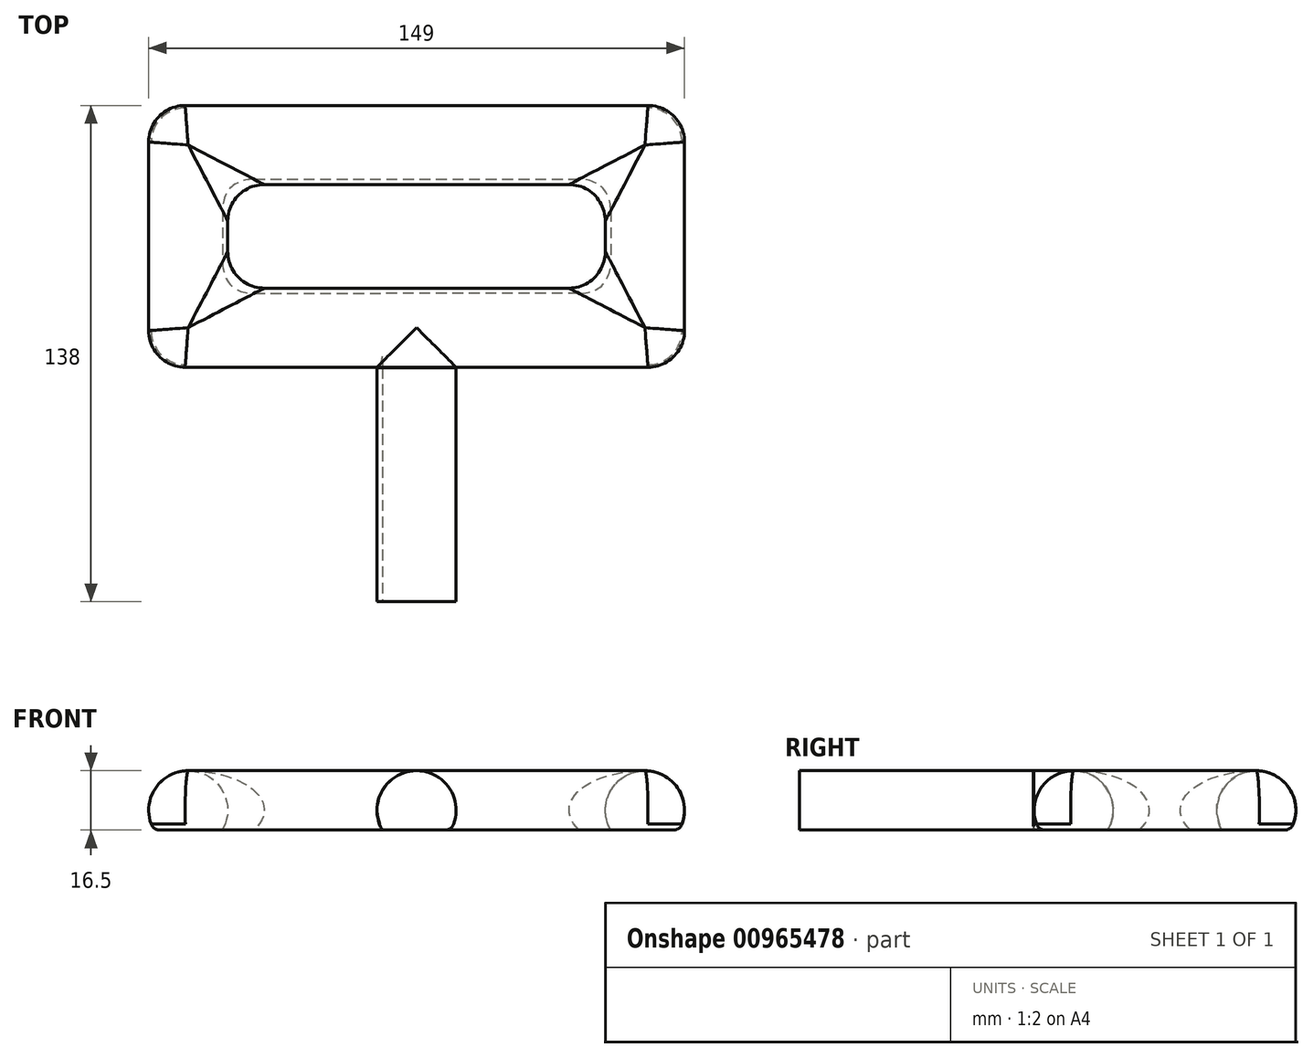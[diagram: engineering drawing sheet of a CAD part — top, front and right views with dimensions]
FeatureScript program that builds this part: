
annotation { "Feature Type Name" : "Feature", "Feature Type Description" : "" }
export const myFeature = defineFeature(function(context is Context, id is Id, definition is map)
    precondition{}
    {
        {
            var Q0;
            Q0=qCreatedBy(makeId("Top.planeOp"),FACE);
            var sketch = newSketch(context, id + "F0", { "sketchPlane" : qUnion([Q0])});
            skLineSegment(sketch, "E0", {"start": v(36.2, -40.03) * mm, "end": v(36.2, 36.17) * mm});
            skLineSegment(sketch, "E1", {"start": v(36.2, 36.17) * mm, "end": v(99.7, 36.17) * mm});
            skLineSegment(sketch, "E2", {"start": v(99.7, 36.17) * mm, "end": v(99.7, 86.97) * mm});
            skLineSegment(sketch, "E3", {"start": v(99.7, 86.97) * mm, "end": v(36.2, 86.97) * mm});
            skLineSegment(sketch, "E4.MirrorCS", {"start": v(36.2, 36.17) * mm, "end": v(-27.3, 36.17) * mm});
            skLineSegment(sketch, "E5.MirrorCS", {"start": v(-27.3, 36.17) * mm, "end": v(-27.3, 86.97) * mm});
            skLineSegment(sketch, "E6.MirrorCS", {"start": v(-27.3, 86.97) * mm, "end": v(36.2, 86.97) * mm});
            skSolve(sketch);
        }
        {
            var Q0;
            Q0=qCreatedBy(makeId("Front.planeOp"),FACE);
            var sketch = newSketch(context, id + "F1", { "sketchPlane" : qUnion([Q0])});
            skPoint(sketch, "E7", {"position": v(36.2, 0) * mm});
            skCircle(sketch, "E8", {"center": v(36.2, 0) * mm, "radius": 11 * mm});
            skLineSegment(sketch, "E9", {"start": v(36.2, 0) * mm, "end": v(36.2, -11) * mm, "construction": true});
            skLineSegment(sketch, "E10", {"start": v(26.68, -5.5) * mm, "end": v(45.73, -5.5) * mm});
            skPoint(sketch, "E10.startSnap0", {"position": v(36.2, -5.5) * mm});
            skPoint(sketch, "E11", {"position": v(29.17, 0) * mm});
            skSolve(sketch);
        }
        {
            var Q0;
            {var subQ0=sQuery(id+"F1.wireOp",EDGE,"E10");Q0=makeQuery(id+"F1.imprint","IMPRINT",FACE,{"disambiguationData":[TD([[makeQuery(id+"F1.imprint","IMPRINT",EDGE,{"derivedFrom":subQ0}),1.0]])]});}
            var Q1;
            Q1=sQuery(id+"F0.wireOp",EDGE,"E0");
            var Q2;
            Q2=sQuery(id+"F0.wireOp",EDGE,"E1");
            var Q3;
            Q3=sQuery(id+"F0.wireOp",EDGE,"E2");
            var Q4;
            Q4=sQuery(id+"F0.wireOp",EDGE,"E3");
            sweep(context, id + "F2", {"profiles" : qUnion([Q0]), "path" : qUnion([Q1, Q2, Q3, Q4])});
        }
        {
            var Q0;
            Q0=qCreatedBy(makeId("Right.planeOp"),FACE);
            cPlane(context, id + "F3", {"entities" : qUnion([Q0]), "cplaneType" : CPlaneType.OFFSET, "offset" : 36.2 * mm, "width" : 152.4 * mm, "height" : 152.4 * mm});
        }
        {
            var Q0;
            Q0=makeQuery(id+"F2.opSweep","SWEPT_BODY",BODY,{"disambiguationData":[OSD([sQuery(id+"F0.wireOp",EDGE,"E3"),sQuery(id+"F1.wireOp",EDGE,"E8"),sQuery(id+"F1.wireOp",EDGE,"E10")])]});
            var Q1;
            Q1=qCreatedBy(id+"F3.planeOp",FACE);
            mirror(context, id + "F4", {"operationType" : NewBodyOperationType.ADD, "entities" : qUnion([Q0]), "mirrorPlane" : qUnion([Q1])});
        }
        {
            var Q0;
            Q0=qCreatedBy(makeId("Front.planeOp"),FACE);
            cPlane(context, id + "F5", {"entities" : qUnion([Q0]), "cplaneType" : CPlaneType.OFFSET, "offset" : 25.12 * mm, "oppositeDirection" : true, "width" : 152.4 * mm, "height" : 152.4 * mm});
        }
        {
            var Q0;
            Q0=qCreatedBy(id+"F5.planeOp",FACE);
            var sketch = newSketch(context, id + "F6", { "sketchPlane" : qUnion([Q0])});
            skCircle(sketch, "E12", {"center": v(36.49, 0) * mm, "radius": 14.97 * mm});
            skLineSegment(sketch, "E13", {"start": v(26.75, -5.42) * mm, "end": v(45.67, -5.42) * mm});
            skArc(sketch, "E14", {"start": v(45.67, -5.42) * mm, "mid": v(36.21, 10.99) * mm, "end": v(26.75, -5.42) * mm});
            skSolve(sketch);
        }
        {
            var Q0;
            Q0=makeQuery(id+"F2.opSweep","MID_CAP_EDGE",EDGE,{"disambiguationData":[OSD([sQuery(id+"F0.wireOp",VERTEX,"E2.start"),sQuery(id+"F1.wireOp",EDGE,"E8")])],"capPos":2.0});
            var Q1;
            Q1=makeQuery(id+"F2.opSweep","MID_CAP_EDGE",EDGE,{"disambiguationData":[OSD([sQuery(id+"F0.wireOp",VERTEX,"E3.start"),sQuery(id+"F1.wireOp",EDGE,"E8")])],"capPos":1.0});
            var Q2;
            Q2=makeQuery(id+"F4.opPattern","COPY",EDGE,{"derivedFrom":makeQuery(id+"F2.opSweep","MID_CAP_EDGE",EDGE,{"disambiguationData":[OSD([sQuery(id+"F0.wireOp",VERTEX,"E3.start"),sQuery(id+"F1.wireOp",EDGE,"E8")])],"capPos":1.0}),"instanceName":"1"});
            var Q3;
            Q3=makeQuery(id+"F4.opPattern","COPY",EDGE,{"derivedFrom":makeQuery(id+"F2.opSweep","MID_CAP_EDGE",EDGE,{"disambiguationData":[OSD([sQuery(id+"F0.wireOp",VERTEX,"E2.start"),sQuery(id+"F1.wireOp",EDGE,"E8")])],"capPos":2.0}),"instanceName":"1"});
            fillet(context, id + "F7", {"entities" : qUnion([Q0, Q1, Q2, Q3]), "radius" : 10.16 * mm, "tangentPropagation" : true, "allowEdgeOverflow" : false});
        }
        {
            var Q0;
            {var subQ0=sQuery(id+"F1.wireOp",EDGE,"E10");var subQ1=sQuery(id+"F1.wireOp",EDGE,"E8");var subQ2=sQuery(id+"F0.wireOp",EDGE,"E3");var subQ3=makeQuery(id+"F2.opSweep","SWEPT_EDGE",EDGE,{"disambiguationData":[OSD([subQ2,subQ1,subQ0]),TDD([subQ2,makeQuery(id+"F1.imprint","INTERSECT",VERTEX,{"disambiguationData":[OD(1.0)],"derivedFrom":[subQ1,subQ0]})])]});Q0=makeQuery(id+"F4.boolean.opBoolean","MERGE",EDGE,{"derivedFrom":[subQ3,makeQuery(id+"F4.opPattern","COPY",EDGE,{"derivedFrom":subQ3,"instanceName":"1"})]});}
            var Q1;
            {var subQ0=sQuery(id+"F1.wireOp",EDGE,"E10");var subQ1=sQuery(id+"F1.wireOp",EDGE,"E8");var subQ2=sQuery(id+"F0.wireOp",EDGE,"E0");Q1=makeQuery(id+"F2.opSweep","SWEPT_EDGE",EDGE,{"disambiguationData":[OSD([subQ2,subQ1,subQ0]),TDD([subQ2,makeQuery(id+"F1.imprint","INTERSECT",VERTEX,{"disambiguationData":[OD(1.0)],"derivedFrom":[subQ1,subQ0]})])]});}
            fillet(context, id + "F8", {"entities" : qUnion([Q0, Q1]), "radius" : 2.54 * mm, "tangentPropagation" : true, "allowEdgeOverflow" : false});
        }
        {
            var Q0;
            Q0=makeQuery(id+"F6.imprint","IMPRINT",FACE,{"disambiguationData":[TD([[makeQuery(id+"F6.imprint","IMPRINT",EDGE,{"derivedFrom":sQuery(id+"F6.wireOp",EDGE,"E12")}),1.0]])]});
            extrude(context, id + "F9", {"entities" : qUnion([Q0]), "operationType" : NewBodyOperationType.REMOVE, "depth" : .1 * mm, "offsetDistance" : 25.4 * mm});
        }
    });
